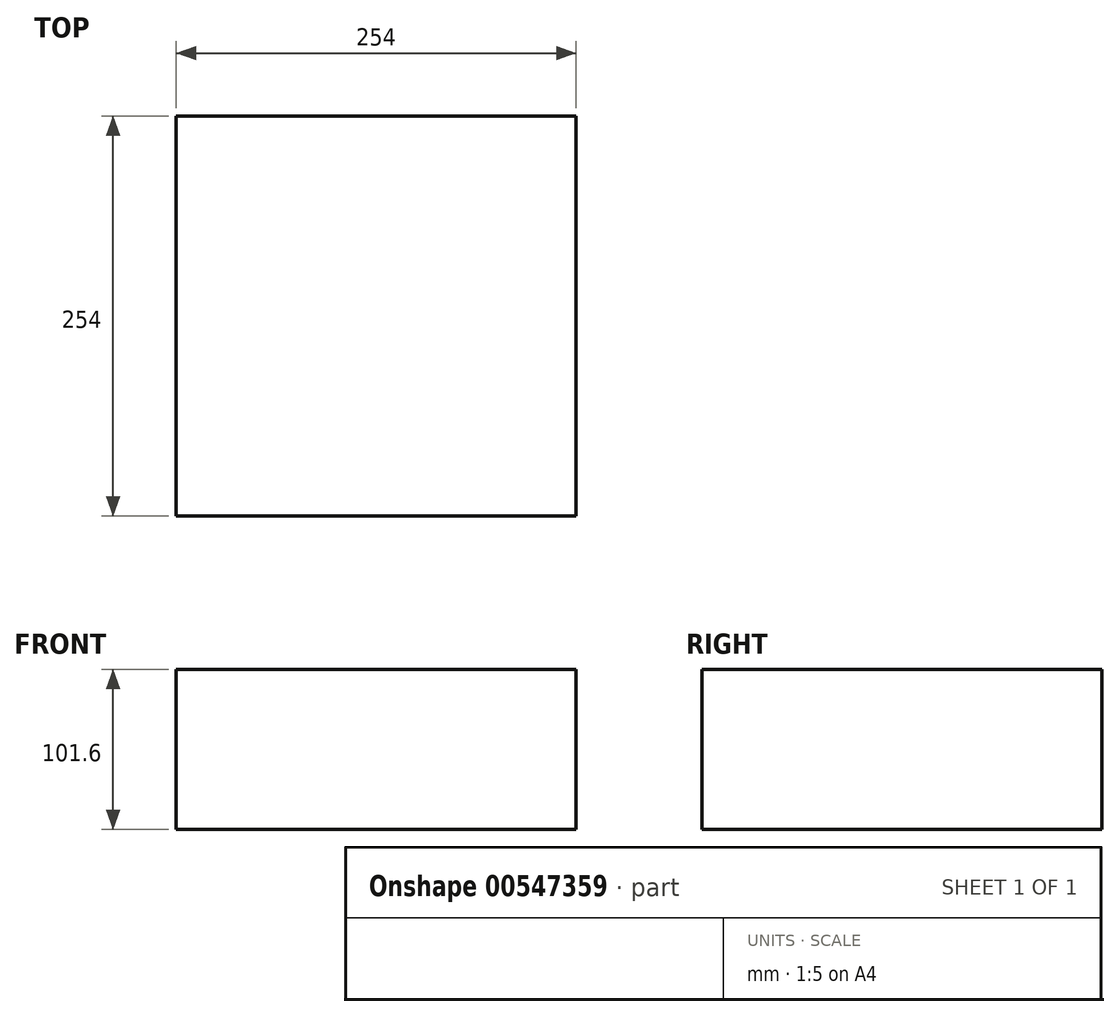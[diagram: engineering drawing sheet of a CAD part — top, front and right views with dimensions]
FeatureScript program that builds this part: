
annotation { "Feature Type Name" : "Feature", "Feature Type Description" : "" }
export const myFeature = defineFeature(function(context is Context, id is Id, definition is map)
    precondition{}
    {
        {
            var Q0;
            Q0=qCreatedBy(makeId("Top.planeOp"),FACE);
            var sketch = newSketch(context, id + "F0", { "sketchPlane" : qUnion([Q0])});
            skLineSegment(sketch, "E0.bottom", {"start": v(127, 127) * mm, "end": v(-127, 127) * mm});
            skLineSegment(sketch, "E0.top", {"start": v(127, -127) * mm, "end": v(-127, -127) * mm});
            skLineSegment(sketch, "E0.left", {"start": v(127, 127) * mm, "end": v(127, -127) * mm});
            skLineSegment(sketch, "E0.right", {"start": v(-127, 127) * mm, "end": v(-127, -127) * mm});
            skPoint(sketch, "E0.middle", {"position": v(0, 0) * mm});
            skSolve(sketch);
        }
        {
            var Q0;
            Q0 = qSketchRegion(id + "F0", true);
            extrude(context, id + "F1", {"entities" : qUnion([Q0]), "depth" : 101.6 * mm, "offsetDistance" : 25.4 * mm});
        }
    });
